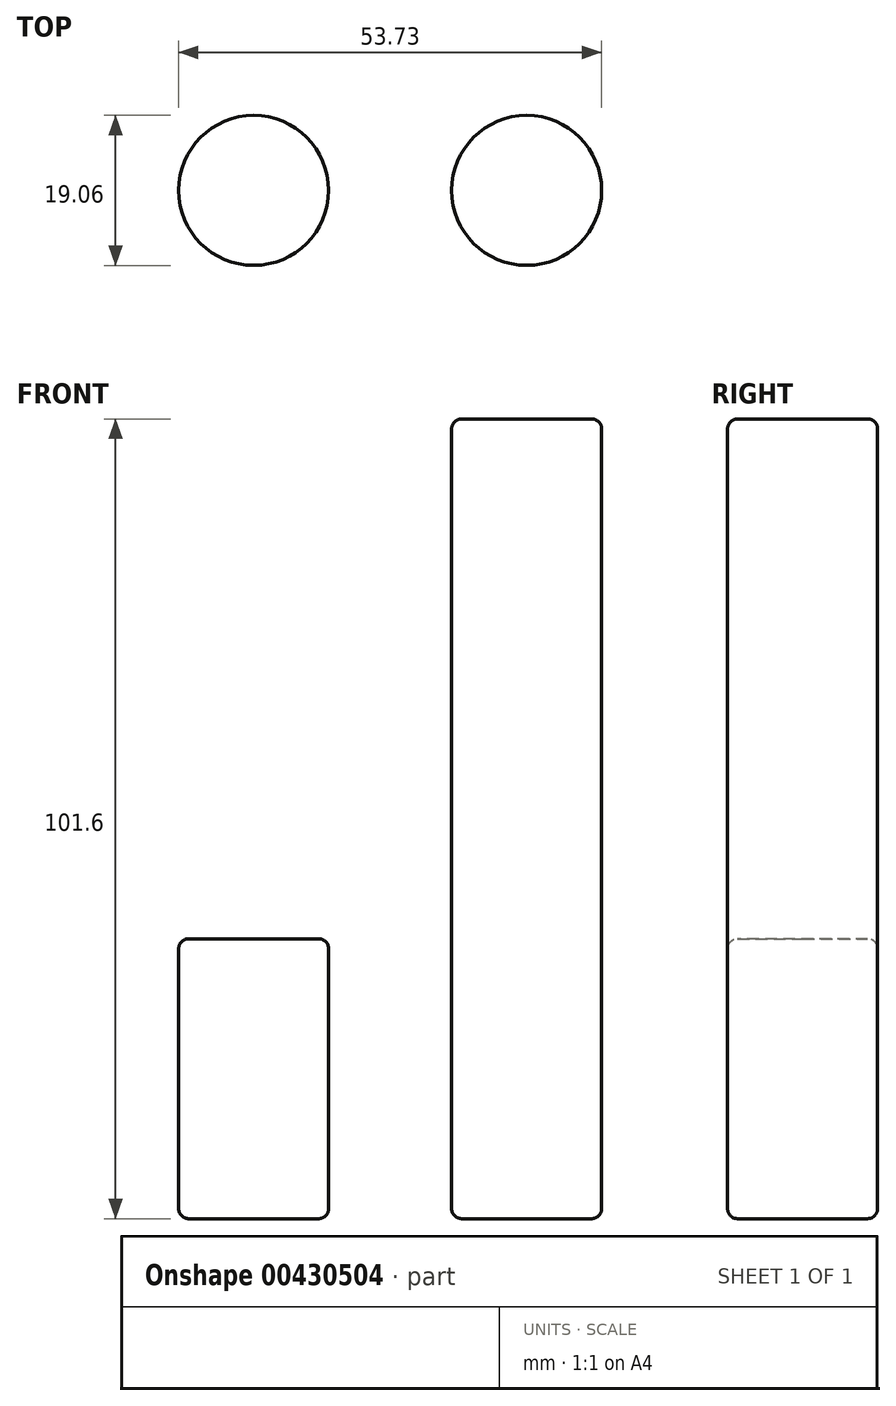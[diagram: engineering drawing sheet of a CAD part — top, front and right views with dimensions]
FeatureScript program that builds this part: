
annotation { "Feature Type Name" : "Feature", "Feature Type Description" : "" }
export const myFeature = defineFeature(function(context is Context, id is Id, definition is map)
    precondition{}
    {
        {
            var Q0;
            Q0=qCreatedBy(makeId("Top.planeOp"),FACE);
            var sketch = newSketch(context, id + "F0", { "sketchPlane" : qUnion([Q0])});
            skCircle(sketch, "E0", {"center": v(0, 0) * mm, "radius": 9.53 * mm});
            skSolve(sketch);
        }
        {
            var Q0;
            Q0 = qSketchRegion(id + "F0", true);
            extrude(context, id + "F1", {"entities" : qUnion([Q0]), "depth" : 35.56 * mm});
        }
        {
            var Q0;
            Q0=makeQuery(id+"F1.opExtrude","CAP_FACE",FACE,{"disambiguationData":[OSD([sQuery(id+"F0.wireOp",EDGE,"E0")])],"isStart":false});
            var Q1;
            Q1=makeQuery(id+"F1.opExtrude","CAP_FACE",FACE,{"disambiguationData":[OSD([sQuery(id+"F0.wireOp",EDGE,"E0")])],"isStart":true});
            fillet(context, id + "F2", {"entities" : qUnion([Q0, Q1]), "radius" : 1.27 * mm, "tangentPropagation" : true, "allowEdgeOverflow" : false});
        }
        {
            var Q0;
            Q0=qCreatedBy(makeId("Top.planeOp"),FACE);
            var sketch = newSketch(context, id + "F3", { "sketchPlane" : qUnion([Q0])});
            skCircle(sketch, "E1", {"center": v(34.68, 0) * mm, "radius": 9.53 * mm});
            skSolve(sketch);
        }
        {
            var Q0;
            Q0=makeQuery(id+"F3.imprint","IMPRINT",FACE,{"disambiguationData":[TD([[makeQuery(id+"F3.imprint","IMPRINT",EDGE,{"derivedFrom":sQuery(id+"F3.wireOp",EDGE,"E1")}),1.0]])]});
            extrude(context, id + "F4", {"entities" : qUnion([Q0]), "depth" : 101.6 * mm});
        }
        {
            var Q0;
            Q0=makeQuery(id+"F4.opExtrude","CAP_FACE",FACE,{"disambiguationData":[OSD([sQuery(id+"F3.wireOp",EDGE,"E1")])],"isStart":false});
            var Q1;
            Q1=makeQuery(id+"F4.opExtrude","CAP_FACE",FACE,{"disambiguationData":[OSD([sQuery(id+"F3.wireOp",EDGE,"E1")])],"isStart":true});
            fillet(context, id + "F5", {"entities" : qUnion([Q0, Q1]), "radius" : 1.27 * mm, "tangentPropagation" : true, "allowEdgeOverflow" : false});
        }
    });
